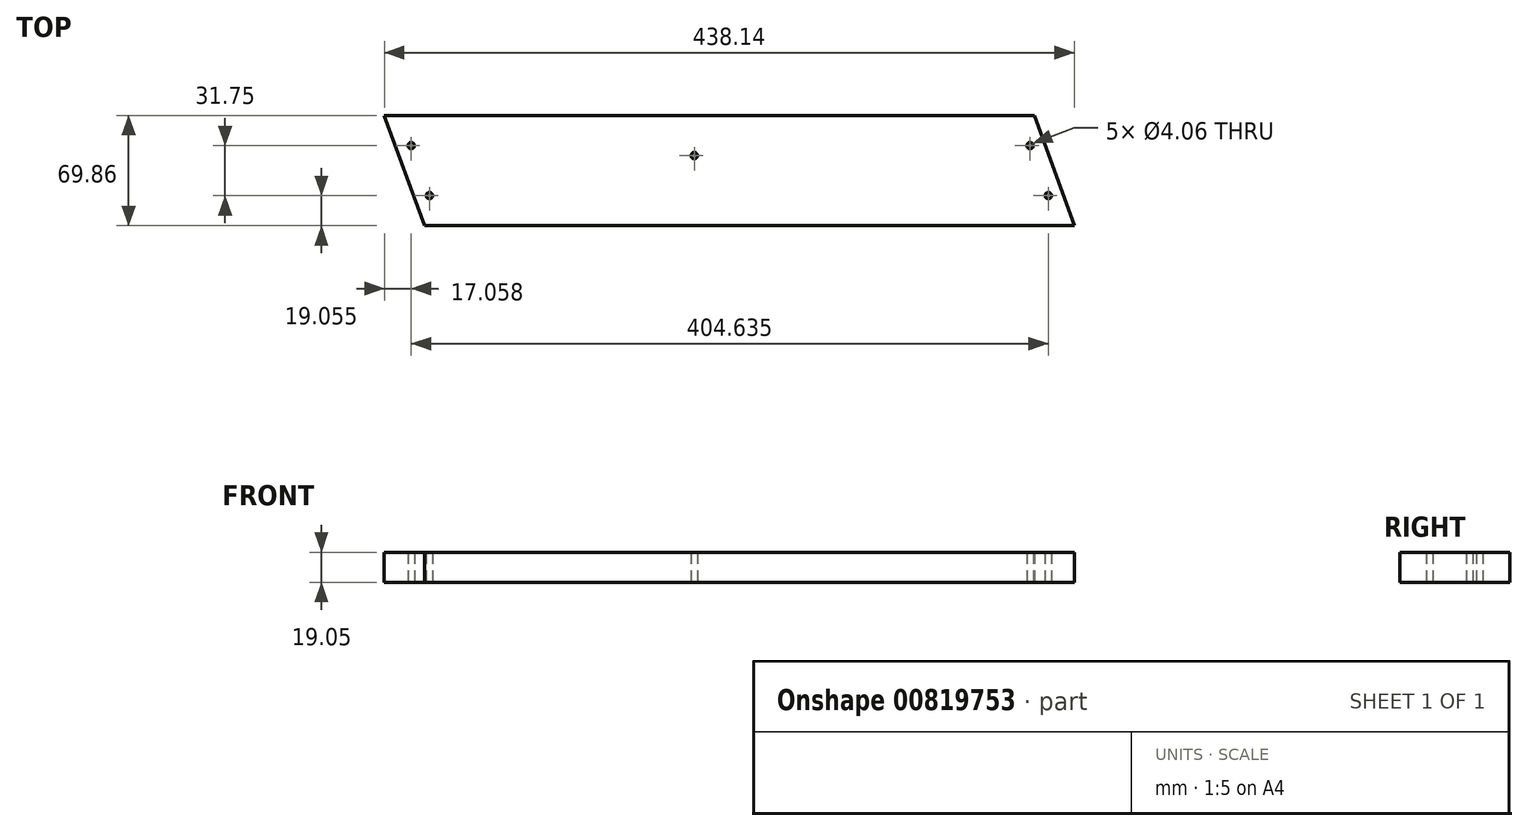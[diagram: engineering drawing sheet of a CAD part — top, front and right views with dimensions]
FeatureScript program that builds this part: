
annotation { "Feature Type Name" : "Feature", "Feature Type Description" : "" }
export const myFeature = defineFeature(function(context is Context, id is Id, definition is map)
    precondition{}
    {
        {
            var Q0;
            Q0=qCreatedBy(makeId("Top.planeOp"),FACE);
            var sketch = newSketch(context, id + "F0", { "sketchPlane" : qUnion([Q0])});
            skLineSegment(sketch, "E0.bottom", {"start": v(219.08, 34.93) * mm, "end": v(-219.08, 34.93) * mm, "construction": true});
            skLineSegment(sketch, "E0.top", {"start": v(219.08, -34.93) * mm, "end": v(-219.08, -34.93) * mm, "construction": true});
            skLineSegment(sketch, "E0.left", {"start": v(219.08, 34.93) * mm, "end": v(219.08, -34.93) * mm, "construction": true});
            skLineSegment(sketch, "E0.right", {"start": v(-219.08, 34.93) * mm, "end": v(-219.08, -34.93) * mm, "construction": true});
            skPoint(sketch, "E0.middle", {"position": v(0, 0) * mm});
            skLineSegment(sketch, "E1", {"start": v(-193.68, 34.93) * mm, "end": v(-193.68, -34.93) * mm, "construction": true});
            skLineSegment(sketch, "E2", {"start": v(193.68, 34.93) * mm, "end": v(193.68, -34.93) * mm, "construction": true});
            skLineSegment(sketch, "E3", {"start": v(-219.08, 34.92) * mm, "end": v(-193.68, -34.92) * mm});
            skLineSegment(sketch, "E4", {"start": v(-193.68, -34.93) * mm, "end": v(219.08, -34.93) * mm});
            skLineSegment(sketch, "E5", {"start": v(219.08, -34.92) * mm, "end": v(193.68, 34.92) * mm});
            skLineSegment(sketch, "E6", {"start": v(193.68, 34.93) * mm, "end": v(-219.08, 34.93) * mm});
            skLineSegment(sketch, "E7", {"start": v(184.15, 34.93) * mm, "end": v(209.55, -34.92) * mm, "construction": true});
            skLineSegment(sketch, "E8", {"start": v(-219.08, 15.87) * mm, "end": v(219.08, 15.88) * mm, "construction": true});
            skLineSegment(sketch, "E9", {"start": v(-219.08, -15.88) * mm, "end": v(219.08, -15.88) * mm, "construction": true});
            skLineSegment(sketch, "E10", {"start": v(-208.94, 34.93) * mm, "end": v(-183.54, -34.93) * mm, "construction": true});
            skCircle(sketch, "E11", {"center": v(-202.01, 15.87) * mm, "radius": 2.03 * mm});
            skCircle(sketch, "E12", {"center": v(-190.47, -15.88) * mm, "radius": 2.03 * mm});
            skCircle(sketch, "E13", {"center": v(191.08, 15.88) * mm, "radius": 2.03 * mm});
            skCircle(sketch, "E14", {"center": v(202.62, -15.88) * mm, "radius": 2.03 * mm});
            skLineSegment(sketch, "E15", {"start": v(-219.08, 9.52) * mm, "end": v(219.08, 9.53) * mm, "construction": true});
            skLineSegment(sketch, "E16", {"start": v(-22.23, 34.93) * mm, "end": v(-22.22, -34.93) * mm, "construction": true});
            skCircle(sketch, "E17", {"center": v(-22.22, 9.52) * mm, "radius": 2.03 * mm});
            skSolve(sketch);
        }
        {
            var Q0;
            Q0=makeQuery(id+"F0.imprint","IMPRINT",FACE,{"disambiguationData":[TD([[makeQuery(id+"F0.imprint","IMPRINT",EDGE,{"derivedFrom":sQuery(id+"F0.wireOp",EDGE,"E3")}),1.0]])]});
            extrude(context, id + "F1", {"entities" : qUnion([Q0]), "depth" : 19.05 * mm, "offsetDistance" : 25.4 * mm});
        }
    });
